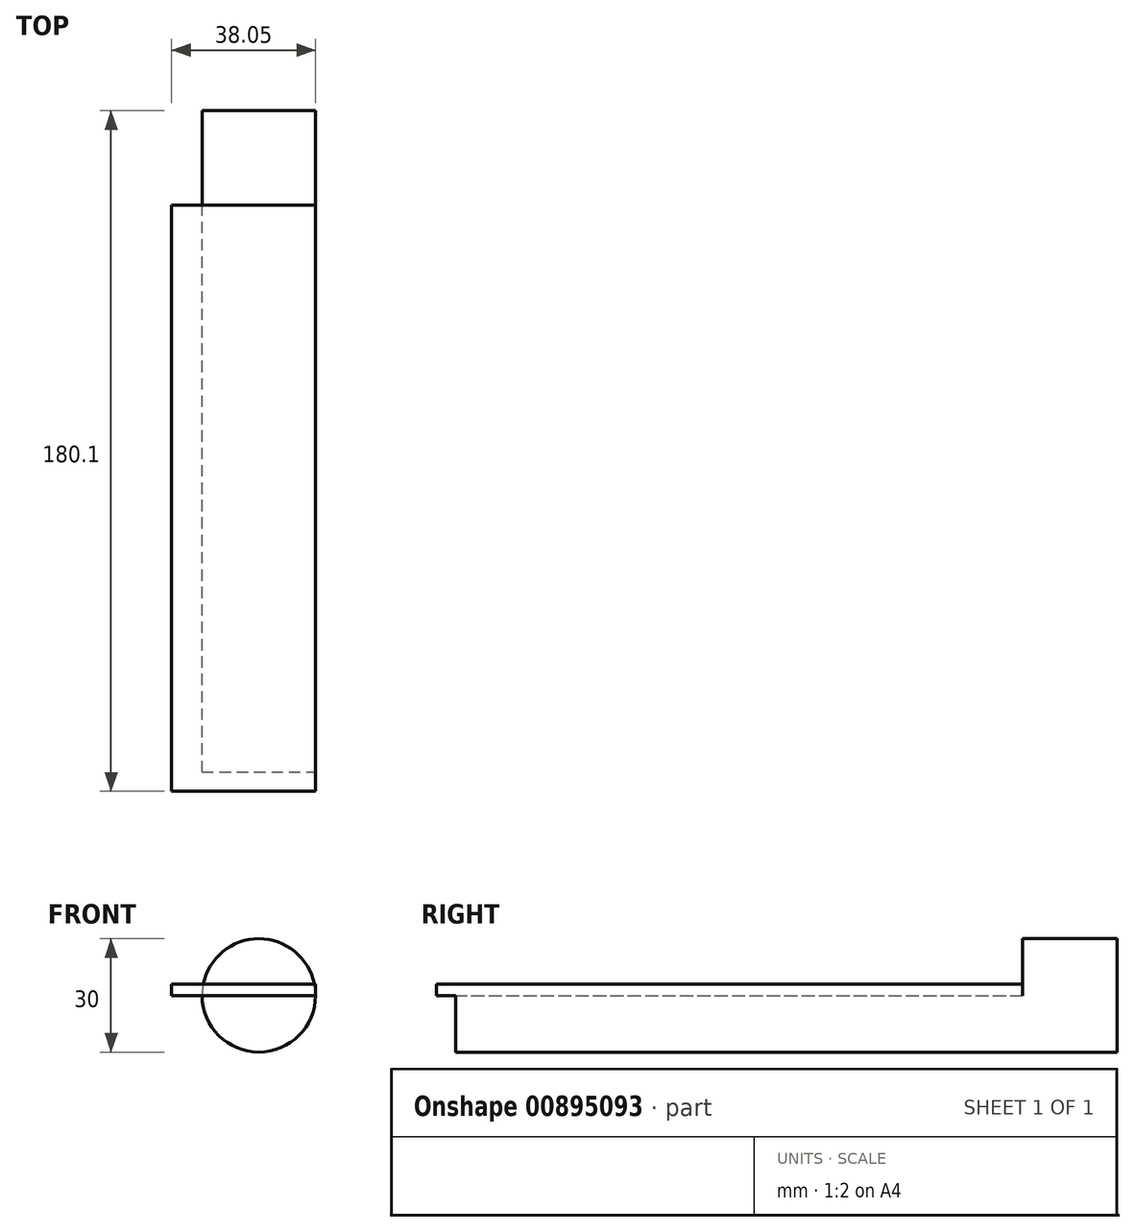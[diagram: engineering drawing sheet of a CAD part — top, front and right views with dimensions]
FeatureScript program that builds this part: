
annotation { "Feature Type Name" : "Feature", "Feature Type Description" : "" }
export const myFeature = defineFeature(function(context is Context, id is Id, definition is map)
    precondition{}
    {
        {
            var Q0;
            Q0=qCreatedBy(makeId("Front.planeOp"),FACE);
            var sketch = newSketch(context, id + "F0", { "sketchPlane" : qUnion([Q0])});
            skArc(sketch, "E0", {"start": v(-15, 0) * mm, "mid": v(0, -15) * mm, "end": v(15, 0) * mm});
            skPoint(sketch, "E1.start.orphan", {"position": v(0, 15) * mm});
            skLineSegment(sketch, "E2", {"start": v(-15, 0) * mm, "end": v(15, 0) * mm});
            skSolve(sketch);
        }
        {
            var Q0;
            Q0 = qSketchRegion(id + "F0", true);
            extrude(context, id + "F1", {"entities" : qUnion([Q0]), "depth" : 150 * mm, "offsetDistance" : 25 * mm});
        }
        {
            var Q0;
            Q0=makeQuery(id+"F1.opExtrude","CAP_FACE",FACE,{"disambiguationData":[OSD([sQuery(id+"F0.wireOp",EDGE,"E0"),sQuery(id+"F0.wireOp",EDGE,"E2")])],"isStart":true});
            cPlane(context, id + "F2", {"entities" : qUnion([Q0]), "cplaneType" : CPlaneType.OFFSET, "offset" : 0 * mm, "width" : 150 * mm, "height" : 150 * mm});
        }
        {
            var Q0;
            Q0=qCreatedBy(makeId("Front.planeOp"),FACE);
            var sketch = newSketch(context, id + "F3", { "sketchPlane" : qUnion([Q0])});
            skCircle(sketch, "E3", {"center": v(0, 0) * mm, "radius": 15 * mm});
            skSolve(sketch);
        }
        {
            var Q0;
            Q0=makeQuery(id+"F3.imprint","IMPRINT",FACE,{"disambiguationData":[TD([[makeQuery(id+"F3.imprint","IMPRINT",EDGE,{"derivedFrom":sQuery(id+"F3.wireOp",EDGE,"E3")}),1.0]])]});
            extrude(context, id + "F4", {"entities" : qUnion([Q0]), "operationType" : NewBodyOperationType.ADD, "oppositeDirection" : true, "depth" : 25 * mm, "offsetDistance" : 25 * mm});
        }
        {
            var Q0;
            Q0=makeQuery(id+"F4.opExtrude","CAP_FACE",FACE,{"disambiguationData":[OSD([sQuery(id+"F3.wireOp",EDGE,"E3")])],"isStart":true});
            var sketch = newSketch(context, id + "F5", { "sketchPlane" : qUnion([Q0])});
            skLineSegment(sketch, "E4.bottom", {"start": v(15, 0) * mm, "end": v(-23.05, 0) * mm});
            skLineSegment(sketch, "E4.top", {"start": v(15, 3) * mm, "end": v(-23.05, 3) * mm});
            skLineSegment(sketch, "E4.left", {"start": v(15, 0) * mm, "end": v(15, 3) * mm});
            skLineSegment(sketch, "E4.right", {"start": v(-23.05, 0) * mm, "end": v(-23.05, 3) * mm});
            skPoint(sketch, "E4.middle", {"position": v(0, 1.5) * mm});
            skPoint(sketch, "E4.middle.positionSnap0", {"position": v(0, 15) * mm});
            skPoint(sketch, "E4.centerSnap0", {"position": v(0, 15) * mm});
            skPoint(sketch, "E5.orphan", {"position": v(-15, 0) * mm});
            skPoint(sketch, "E6.orphan", {"position": v(-15, 3) * mm});
            skSolve(sketch);
        }
        {
            var Q0;
            Q0 = qSketchRegion(id + "F5", true);
            extrude(context, id + "F6", {"entities" : qUnion([Q0]), "operationType" : NewBodyOperationType.ADD, "depth" : 155.1 * mm, "offsetDistance" : 25 * mm});
        }
    });
